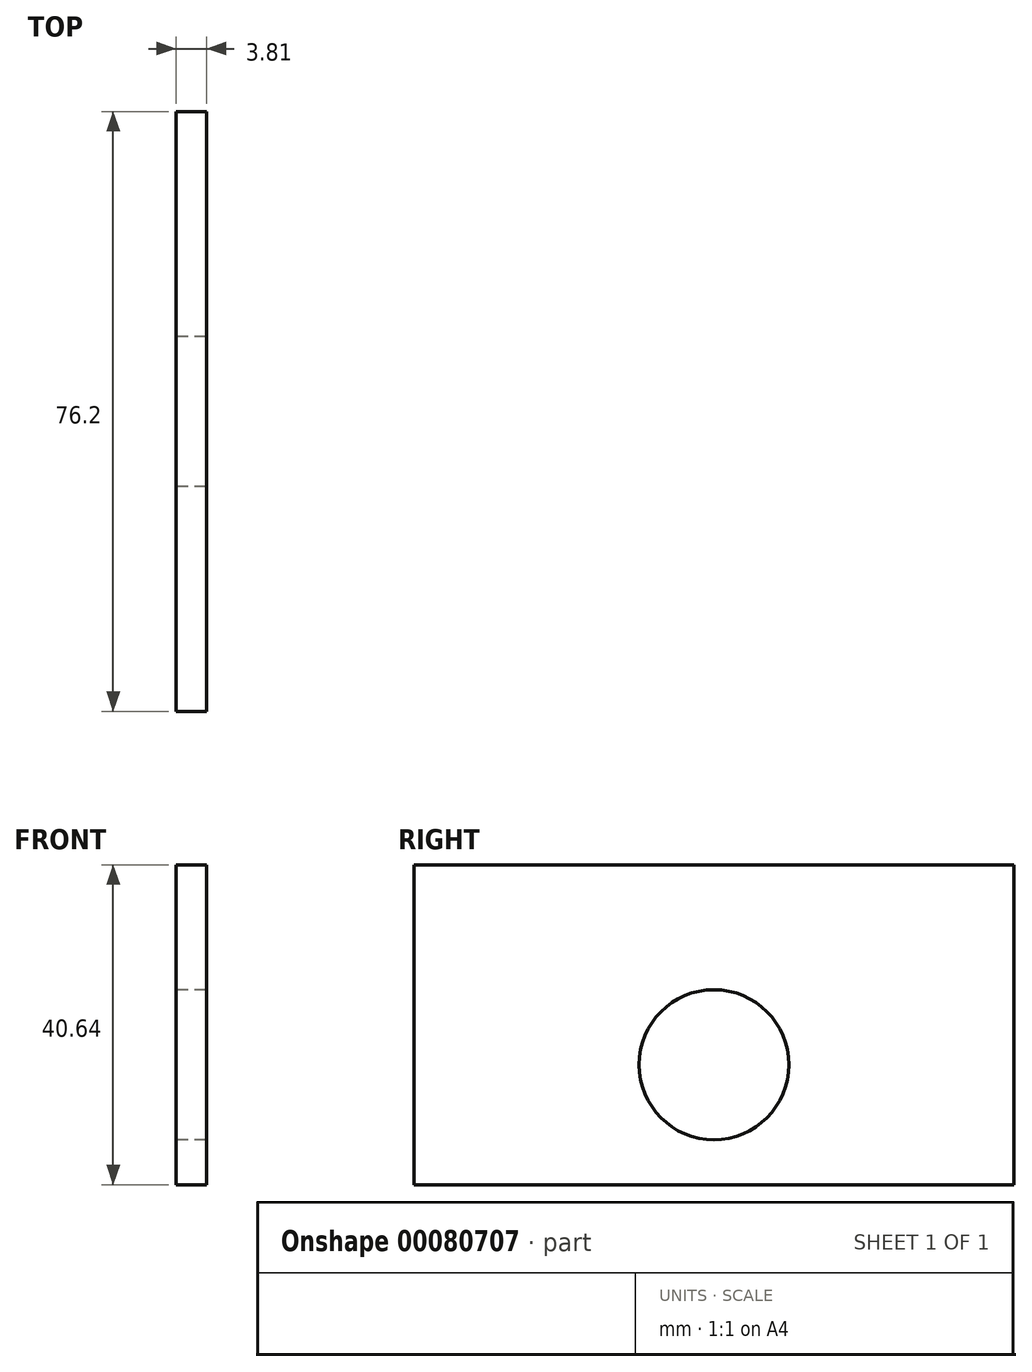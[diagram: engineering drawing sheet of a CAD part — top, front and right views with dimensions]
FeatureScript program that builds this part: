
annotation { "Feature Type Name" : "Feature", "Feature Type Description" : "" }
export const myFeature = defineFeature(function(context is Context, id is Id, definition is map)
    precondition{}
    {
        {
            var Q0;
            Q0=qCreatedBy(makeId("Right.planeOp"),FACE);
            var sketch = newSketch(context, id + "F0", { "sketchPlane" : qUnion([Q0])});
            skLineSegment(sketch, "E0.bottom", {"start": v(38.1, -20.32) * mm, "end": v(-38.1, -20.32) * mm});
            skLineSegment(sketch, "E0.top", {"start": v(38.1, 20.32) * mm, "end": v(-38.1, 20.32) * mm});
            skLineSegment(sketch, "E0.left", {"start": v(38.1, -20.32) * mm, "end": v(38.1, 20.32) * mm});
            skLineSegment(sketch, "E0.right", {"start": v(-38.1, -20.32) * mm, "end": v(-38.1, 20.32) * mm});
            skPoint(sketch, "E0.middle", {"position": v(0, 0) * mm});
            skLineSegment(sketch, "E1", {"start": v(0, 0) * mm, "end": v(0, -5.08) * mm, "construction": true});
            skCircle(sketch, "E2", {"center": v(0, -5.08) * mm, "radius": 9.53 * mm});
            skSolve(sketch);
        }
        {
            var Q0;
            Q0=makeQuery(id+"F0.imprint","IMPRINT",FACE,{"disambiguationData":[TD([[makeQuery(id+"F0.imprint","IMPRINT",EDGE,{"derivedFrom":sQuery(id+"F0.wireOp",EDGE,"E0.bottom")}),-1.0]])]});
            extrude(context, id + "F1", {"entities" : qUnion([Q0]), "depth" : 3.8 * mm});
        }
    });
